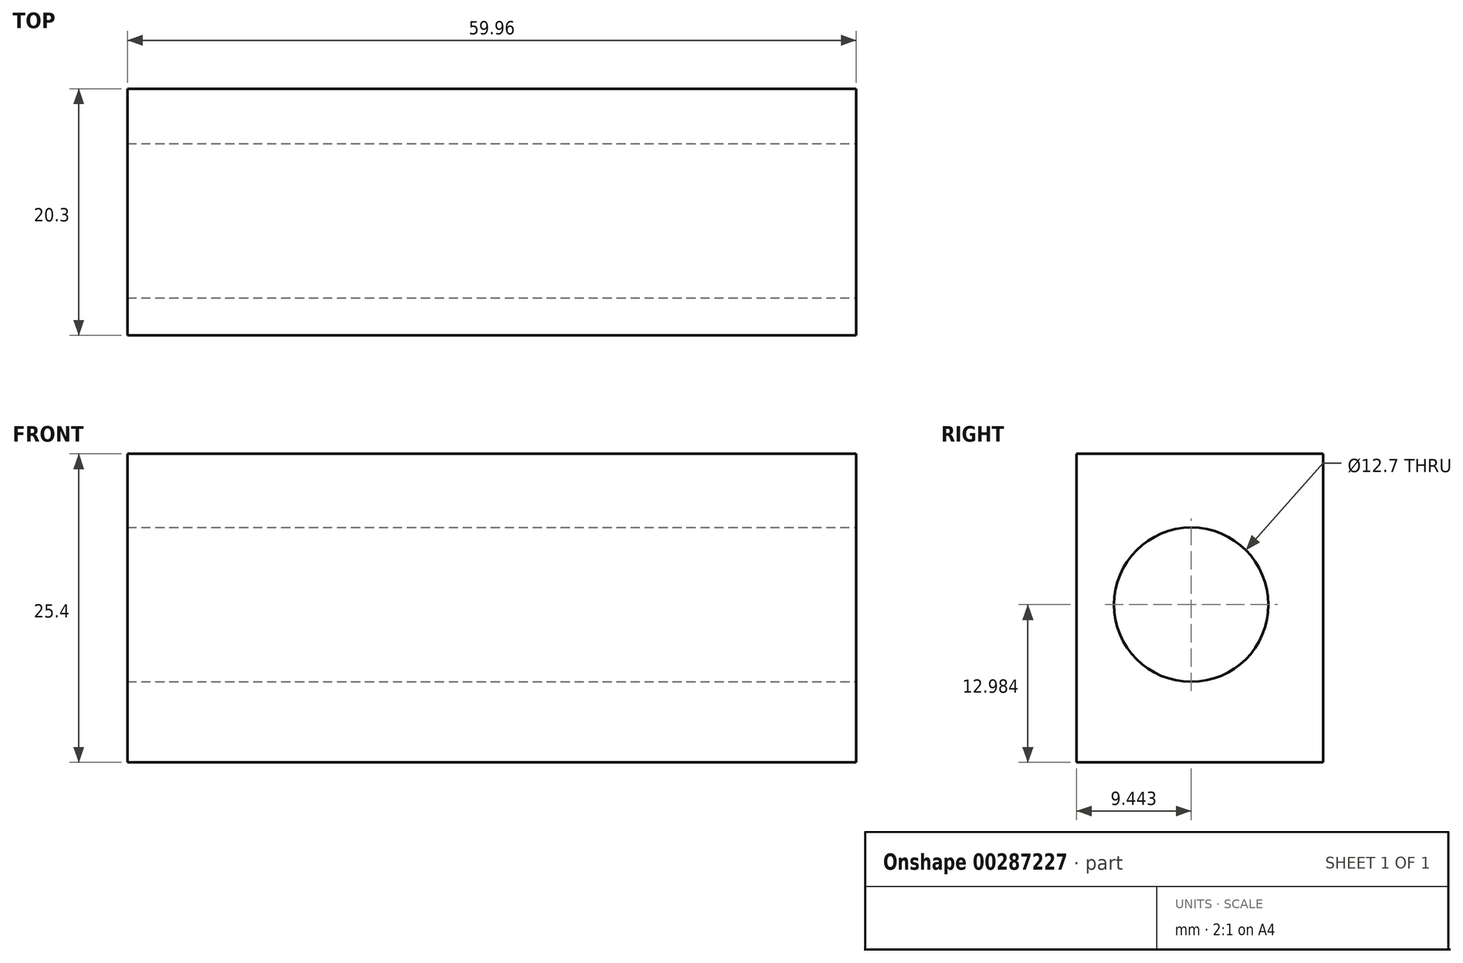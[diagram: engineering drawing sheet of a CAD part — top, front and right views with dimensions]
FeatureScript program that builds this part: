
annotation { "Feature Type Name" : "Feature", "Feature Type Description" : "" }
export const myFeature = defineFeature(function(context is Context, id is Id, definition is map)
    precondition{}
    {
        {
            var Q0;
            Q0=qCreatedBy(makeId("Top.planeOp"),FACE);
            var sketch = newSketch(context, id + "F0", { "sketchPlane" : qUnion([Q0])});
            skLineSegment(sketch, "E0.bottom", {"start": v(0, 20.3) * mm, "end": v(59.96, 20.3) * mm});
            skLineSegment(sketch, "E0.top", {"start": v(0, 0) * mm, "end": v(59.96, 0) * mm});
            skLineSegment(sketch, "E0.left", {"start": v(0, 20.3) * mm, "end": v(0, 0) * mm});
            skLineSegment(sketch, "E0.right", {"start": v(59.96, 20.3) * mm, "end": v(59.96, 0) * mm});
            skSolve(sketch);
        }
        {
            var Q0;
            Q0 = qSketchRegion(id + "F0", true);
            extrude(context, id + "F1", {"entities" : qUnion([Q0]), "depth" : 25.4 * mm});
        }
        {
            var Q0;
            Q0=makeQuery(id+"F1.opExtrude","SWEPT_FACE",FACE,{"disambiguationData":[OSD([sQuery(id+"F0.wireOp",EDGE,"E0.right")])]});
            var sketch = newSketch(context, id + "F2", { "sketchPlane" : qUnion([Q0])});
            skPoint(sketch, "E1", {"position": v(9.44, 12.98) * mm});
            skSolve(sketch);
        }
        {
            var Q0;
            Q0=sQuery(id+"F2.wireOp",VERTEX,"E1");
            var Q1;
            Q1=makeQuery(id+"F1.opExtrude","SWEPT_BODY",BODY,{"disambiguationData":[OSD([sQuery(id+"F0.wireOp",EDGE,"E0.bottom"),sQuery(id+"F0.wireOp",EDGE,"E0.top"),sQuery(id+"F0.wireOp",EDGE,"E0.left"),sQuery(id+"F0.wireOp",EDGE,"E0.right")])]});
            hole(context, id + "F3", {"style" : HoleStyle.SIMPLE, "endStyle" : HoleEndStyle.THROUGH, "holeDiameter" : 12.7 * mm, "tappedDepth" : 12.7 * mm, "tapClearance" : 3, "locations" : qUnion([Q0]), "scope" : qUnion([Q1])});
        }
    });
